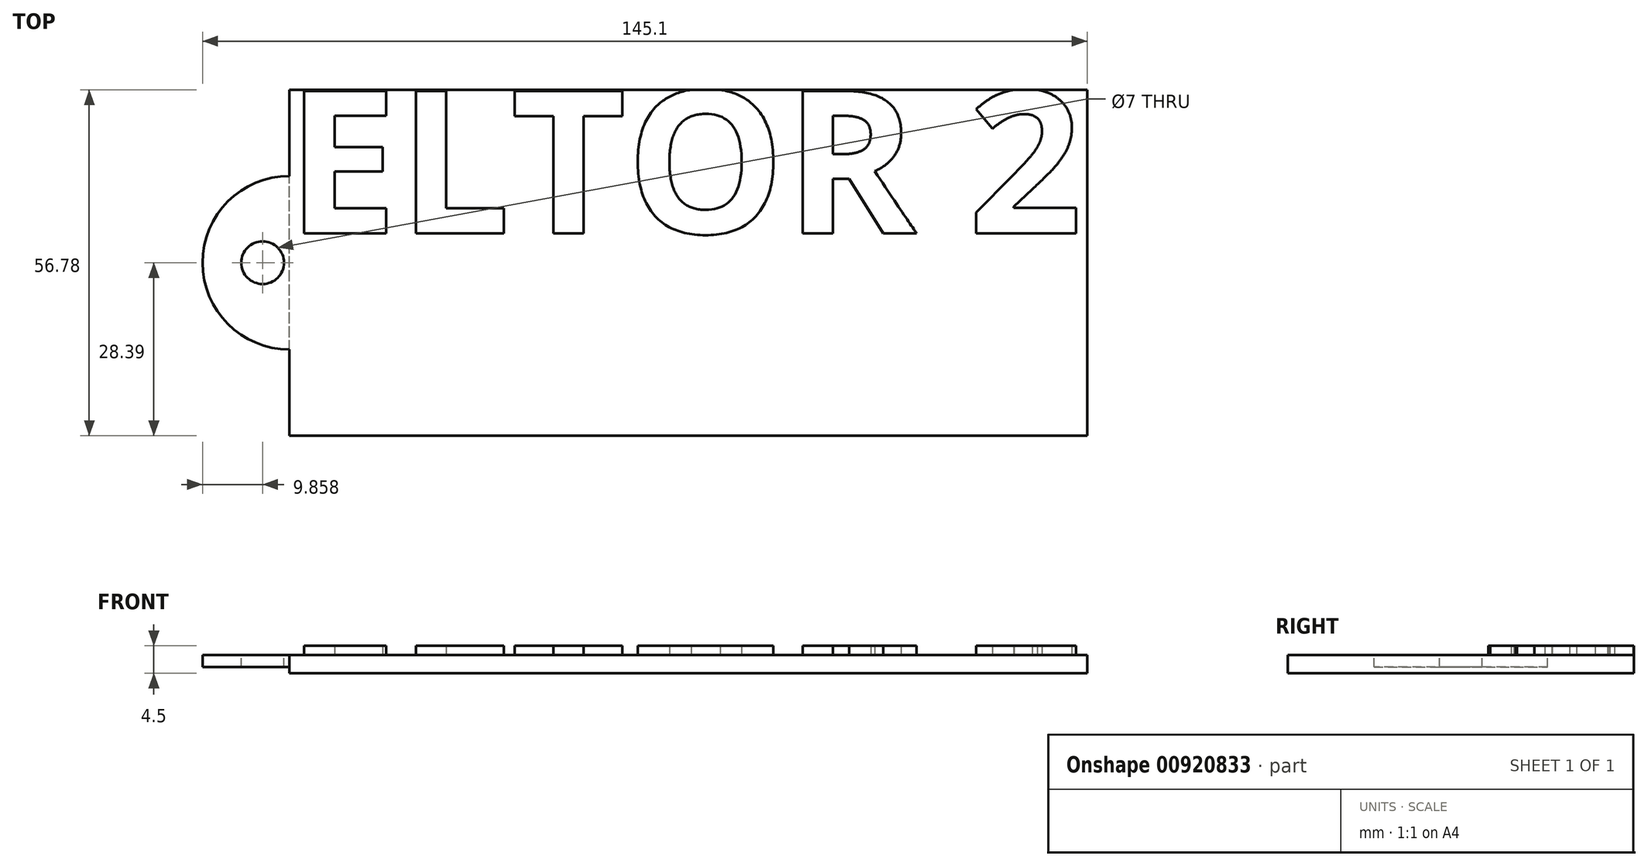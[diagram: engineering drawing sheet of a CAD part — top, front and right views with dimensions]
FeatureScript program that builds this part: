
annotation { "Feature Type Name" : "Feature", "Feature Type Description" : "" }
export const myFeature = defineFeature(function(context is Context, id is Id, definition is map)
    precondition{}
    {
        {
            var Q0;
            Q0=qCreatedBy(makeId("Top.planeOp"),FACE);
            var sketch = newSketch(context, id + "F0", { "sketchPlane" : qUnion([Q0])});
            skLineSegment(sketch, "E0.bottom", {"start": v(65.43, -28.39) * mm, "end": v(-65.43, -28.39) * mm});
            skLineSegment(sketch, "E0.top", {"start": v(65.43, 28.39) * mm, "end": v(-65.43, 28.39) * mm});
            skLineSegment(sketch, "E0.left", {"start": v(65.43, -28.39) * mm, "end": v(65.43, 28.39) * mm});
            skLineSegment(sketch, "E0.right", {"start": v(-65.43, -28.39) * mm, "end": v(-65.43, 28.39) * mm});
            skPoint(sketch, "E0.middle", {"position": v(0, 0) * mm});
            skSolve(sketch);
        }
        {
            var Q0;
            Q0=makeQuery(id+"F0.imprint","IMPRINT",FACE,{"disambiguationData":[TD([[makeQuery(id+"F0.imprint","IMPRINT",EDGE,{"derivedFrom":sQuery(id+"F0.wireOp",EDGE,"E0.bottom")}),-1.0]])]});
            var Q1;
            Q1 = qSketchRegion(id + "F2", true);
            extrude(context, id + "F1", {"entities" : qUnion([Q0, Q1]), "depth" : 3 * mm, "offsetDistance" : 25 * mm});
        }
        {
            var Q0;
            Q0=makeQuery(id+"F1.opExtrude","CAP_FACE",FACE,{"disambiguationData":[OSD([sQuery(id+"F0.wireOp",EDGE,"E0.bottom"),sQuery(id+"F0.wireOp",EDGE,"E0.top"),sQuery(id+"F0.wireOp",EDGE,"E0.left"),sQuery(id+"F0.wireOp",EDGE,"E0.right")])],"isStart":false});
            var sketch = newSketch(context, id + "F2", { "sketchPlane" : qUnion([Q0])});
            skText(sketch, "E1", { "text": "ELTOR 2", "fontName": "OpenSans-Bold.ttf"});
            const initialGuessF2  = {"E1": [-0.06592, 0.00484, 1, 0, 0.02355]};
            skSetInitialGuess(sketch, initialGuessF2);
            skSolve(sketch);
        }
        {
            var Q0;
            Q0=makeQuery(id+"F2.imprint","IMPRINT",FACE,{"disambiguationData":[TD([[makeQuery(id+"F2.imprint","IMPRINT",EDGE,{"derivedFrom":sQuery(id+"F2.wireOp",EDGE,"E1.sketch_text.stroke-59")}),-1.0]])]});
            var Q1;
            Q1=makeQuery(id+"F2.imprint","IMPRINT",FACE,{"disambiguationData":[TD([[makeQuery(id+"F2.imprint","IMPRINT",EDGE,{"derivedFrom":sQuery(id+"F2.wireOp",EDGE,"E1.sketch_text.stroke-40")}),-1.0]])]});
            var Q2;
            Q2=makeQuery(id+"F2.imprint","IMPRINT",FACE,{"disambiguationData":[TD([[makeQuery(id+"F2.imprint","IMPRINT",EDGE,{"derivedFrom":sQuery(id+"F2.wireOp",EDGE,"E1.sketch_text.stroke-26")}),-1.0]])]});
            var Q3;
            Q3=makeQuery(id+"F2.imprint","IMPRINT",FACE,{"disambiguationData":[TD([[makeQuery(id+"F2.imprint","IMPRINT",EDGE,{"derivedFrom":sQuery(id+"F2.wireOp",EDGE,"E1.sketch_text.stroke-18")}),-1.0]])]});
            var Q4;
            Q4=makeQuery(id+"F2.imprint","IMPRINT",FACE,{"disambiguationData":[TD([[makeQuery(id+"F2.imprint","IMPRINT",EDGE,{"derivedFrom":sQuery(id+"F2.wireOp",EDGE,"E1.sketch_text.stroke-12")}),-1.0]])]});
            var Q5;
            Q5=makeQuery(id+"F2.imprint","IMPRINT",FACE,{"disambiguationData":[TD([[makeQuery(id+"F2.imprint","IMPRINT",EDGE,{"derivedFrom":sQuery(id+"F2.wireOp",EDGE,"E1.sketch_text.stroke-0")}),-1.0]])]});
            extrude(context, id + "F3", {"entities" : qUnion([Q0, Q1, Q2, Q3, Q4, Q5]), "operationType" : NewBodyOperationType.ADD, "depth" : 1.5 * mm, "offsetDistance" : 25 * mm});
        }
        {
            var Q0;
            {var subQ2=sQuery(id+"F0.wireOp",EDGE,"E0.bottom");var subQ3=sQuery(id+"F0.wireOp",EDGE,"E0.top");var subQ4=sQuery(id+"F0.wireOp",EDGE,"E0.left");var subQ5=sQuery(id+"F0.wireOp",EDGE,"E0.right");Q0=makeQuery(id+"F3.boolean.opBoolean","SPLIT",FACE,{"disambiguationData":[TD([makeQuery(id+"F1.opExtrude","SWEPT_FACE",FACE,{"disambiguationData":[OSD([subQ2])]})])],"derivedFrom":makeQuery(id+"F1.opExtrude","CAP_FACE",FACE,{"disambiguationData":[OSD([subQ2,subQ3,subQ4,subQ5])],"isStart":false})});}
            var sketch = newSketch(context, id + "F4", { "sketchPlane" : qUnion([Q0])});
            skCircle(sketch, "E2", {"center": v(-65.43, 0) * mm, "radius": 14.24 * mm});
            skSolve(sketch);
        }
        {
            var Q0;
            Q0 = qSketchRegion(id + "F4", true);
            extrude(context, id + "F5", {"entities" : qUnion([Q0]), "operationType" : NewBodyOperationType.ADD, "oppositeDirection" : true, "depth" : 2 * mm, "offsetDistance" : 25 * mm});
        }
        {
            var Q0;
            {var subQ2=sQuery(id+"F0.wireOp",EDGE,"E0.bottom");var subQ3=sQuery(id+"F0.wireOp",EDGE,"E0.top");var subQ4=sQuery(id+"F0.wireOp",EDGE,"E0.left");var subQ5=sQuery(id+"F0.wireOp",EDGE,"E0.right");Q0=makeQuery(id+"F5.boolean.opBoolean","MERGE",FACE,{"derivedFrom":[makeQuery(id+"F3.boolean.opBoolean","SPLIT",FACE,{"disambiguationData":[TD([makeQuery(id+"F1.opExtrude","SWEPT_FACE",FACE,{"disambiguationData":[OSD([subQ2])]})])],"derivedFrom":makeQuery(id+"F1.opExtrude","CAP_FACE",FACE,{"disambiguationData":[OSD([subQ2,subQ3,subQ4,subQ5])],"isStart":false})}),makeQuery(id+"F5.opExtrude","CAP_FACE",FACE,{"disambiguationData":[OSD([sQuery(id+"F4.wireOp",EDGE,"E2")])],"isStart":true})]});}
            var sketch = newSketch(context, id + "F6", { "sketchPlane" : qUnion([Q0])});
            skCircle(sketch, "E3", {"center": v(-69.81, 0) * mm, "radius": 5.6 * mm});
            skSolve(sketch);
        }
        {
            var Q0;
            Q0=sQuery(id+"F6.wireOp",VERTEX,"E3.center");
            var Q1;
            Q1=makeQuery(id+"F1.opExtrude","SWEPT_BODY",BODY,{"disambiguationData":[OSD([sQuery(id+"F0.wireOp",EDGE,"E0.bottom"),sQuery(id+"F0.wireOp",EDGE,"E0.top"),sQuery(id+"F0.wireOp",EDGE,"E0.left"),sQuery(id+"F0.wireOp",EDGE,"E0.right")])]});
            hole(context, id + "F7", {"style" : HoleStyle.SIMPLE, "endStyle" : HoleEndStyle.THROUGH, "holeDiameter" : 7 * mm, "majorDiameter" : 5 * mm, "isTappedThrough" : true, "tappedDepth" : 12 * mm, "tapClearance" : 3, "locations" : qUnion([Q0]), "scope" : qUnion([Q1])});
        }
    });
